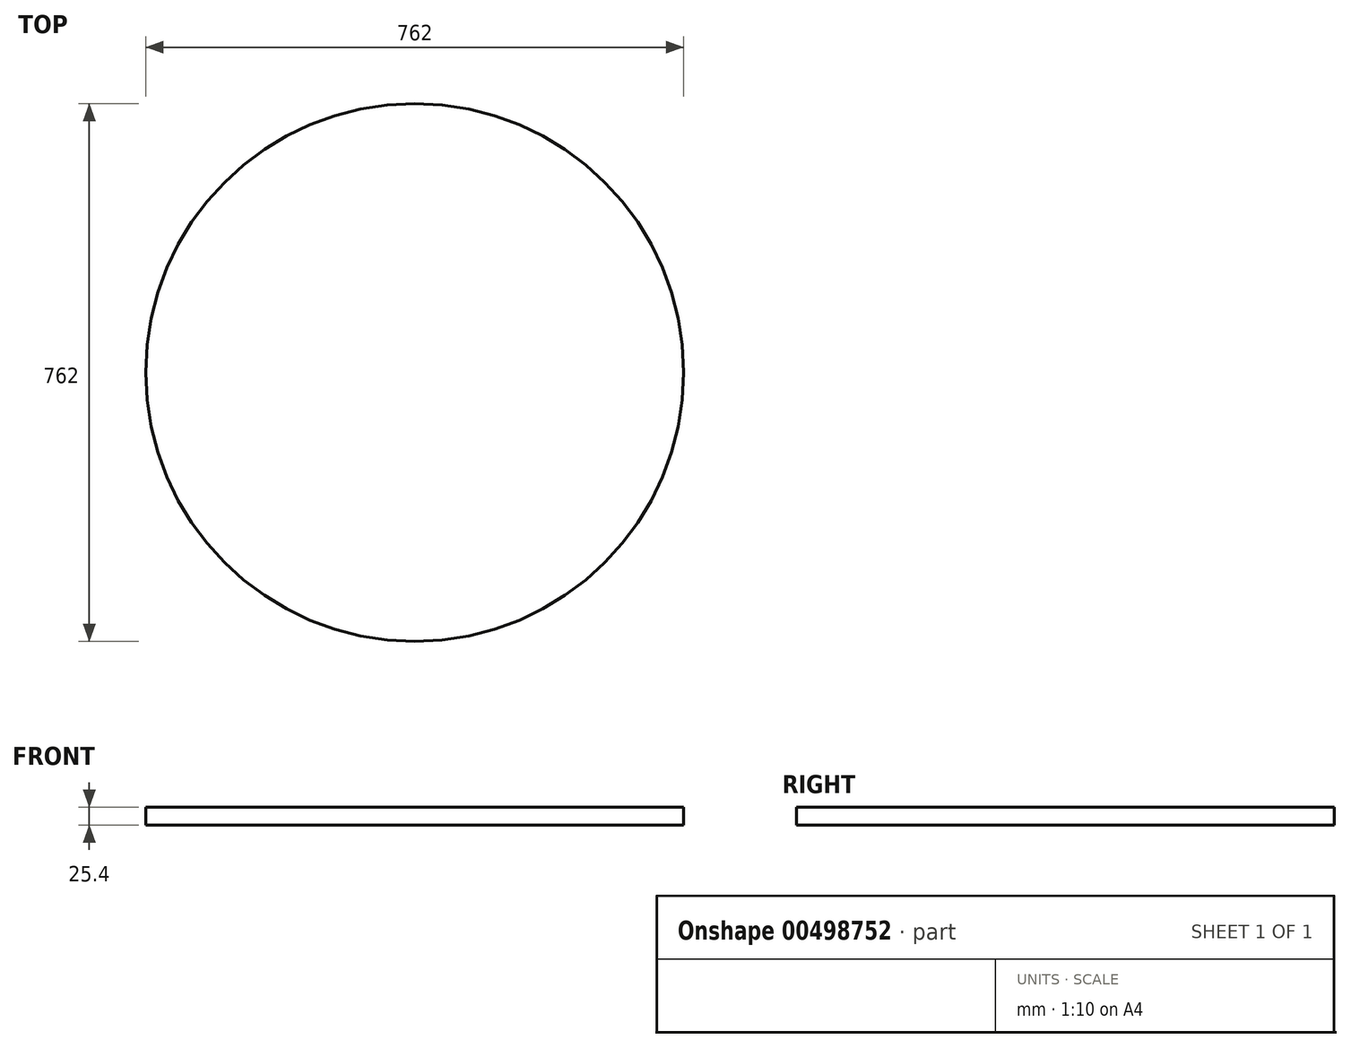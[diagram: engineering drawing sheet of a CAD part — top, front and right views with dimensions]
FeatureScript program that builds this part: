
annotation { "Feature Type Name" : "Feature", "Feature Type Description" : "" }
export const myFeature = defineFeature(function(context is Context, id is Id, definition is map)
    precondition{}
    {
        {
            var Q0;
            Q0=qCreatedBy(makeId("Top.planeOp"),FACE);
            var sketch = newSketch(context, id + "F0", { "sketchPlane" : qUnion([Q0])});
            skCircle(sketch, "E0", {"center": v(0, 0) * mm, "radius": 381 * mm});
            skSolve(sketch);
        }
        {
            var Q0;
            Q0 = qSketchRegion(id + "F0", true);
            extrude(context, id + "F1", {"entities" : qUnion([Q0]), "depth" : 25.4 * mm});
        }
    });
